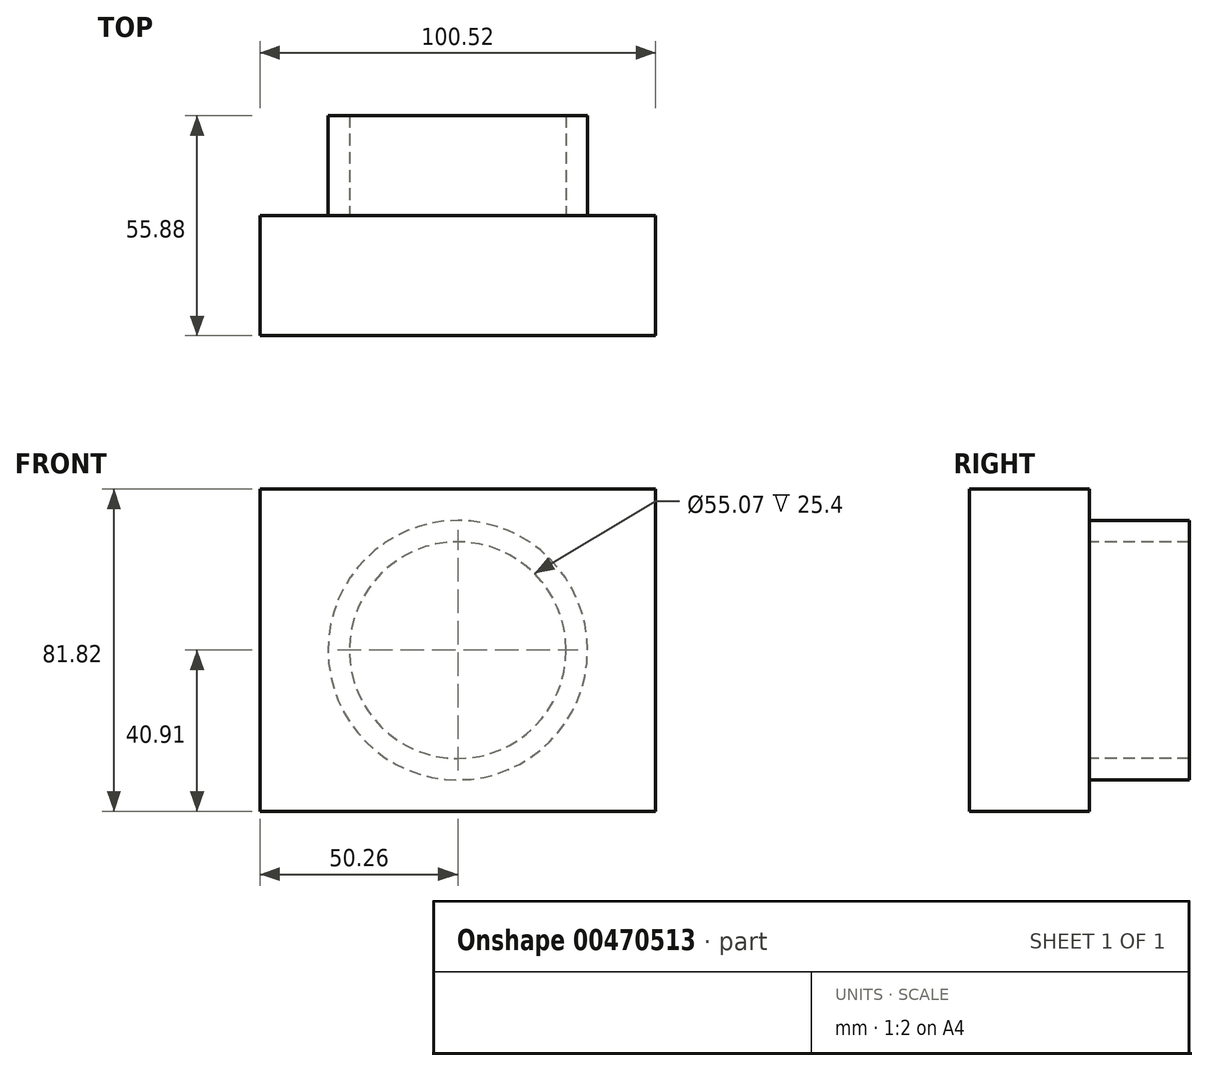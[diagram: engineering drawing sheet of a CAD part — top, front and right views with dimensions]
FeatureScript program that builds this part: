
annotation { "Feature Type Name" : "Feature", "Feature Type Description" : "" }
export const myFeature = defineFeature(function(context is Context, id is Id, definition is map)
    precondition{}
    {
        {
            var Q0;
            Q0=qCreatedBy(makeId("Front.planeOp"),FACE);
            var sketch = newSketch(context, id + "F0", { "sketchPlane" : qUnion([Q0])});
            skLineSegment(sketch, "E0.bottom", {"start": v(50.26, -40.9) * mm, "end": v(-50.26, -40.9) * mm});
            skLineSegment(sketch, "E0.top", {"start": v(50.26, 40.9) * mm, "end": v(-50.26, 40.9) * mm});
            skLineSegment(sketch, "E0.left", {"start": v(50.26, -40.9) * mm, "end": v(50.26, 40.9) * mm});
            skLineSegment(sketch, "E0.right", {"start": v(-50.26, -40.9) * mm, "end": v(-50.26, 40.9) * mm});
            skPoint(sketch, "E0.middle", {"position": v(0, 0) * mm});
            skSolve(sketch);
        }
        {
            var Q0;
            Q0=makeQuery(id+"F0.imprint","IMPRINT",FACE,{"disambiguationData":[TD([[makeQuery(id+"F0.imprint","IMPRINT",EDGE,{"derivedFrom":sQuery(id+"F0.wireOp",EDGE,"E0.bottom")}),-1.0]])]});
            extrude(context, id + "F1", {"entities" : qUnion([Q0]), "depth" : 30.48 * mm});
        }
        {
            var Q0;
            Q0=qCreatedBy(makeId("Front.planeOp"),FACE);
            var sketch = newSketch(context, id + "F2", { "sketchPlane" : qUnion([Q0])});
            skCircle(sketch, "E1", {"center": v(0, 0) * mm, "radius": 32.95 * mm});
            skCircle(sketch, "E2", {"center": v(0, 0) * mm, "radius": 27.53 * mm});
            skSolve(sketch);
        }
        {
            var Q0;
            Q0 = qSketchRegion(id + "F2", true);
            extrude(context, id + "F3", {"entities" : qUnion([Q0]), "operationType" : NewBodyOperationType.ADD, "oppositeDirection" : true, "depth" : 25.4 * mm});
        }
    });
